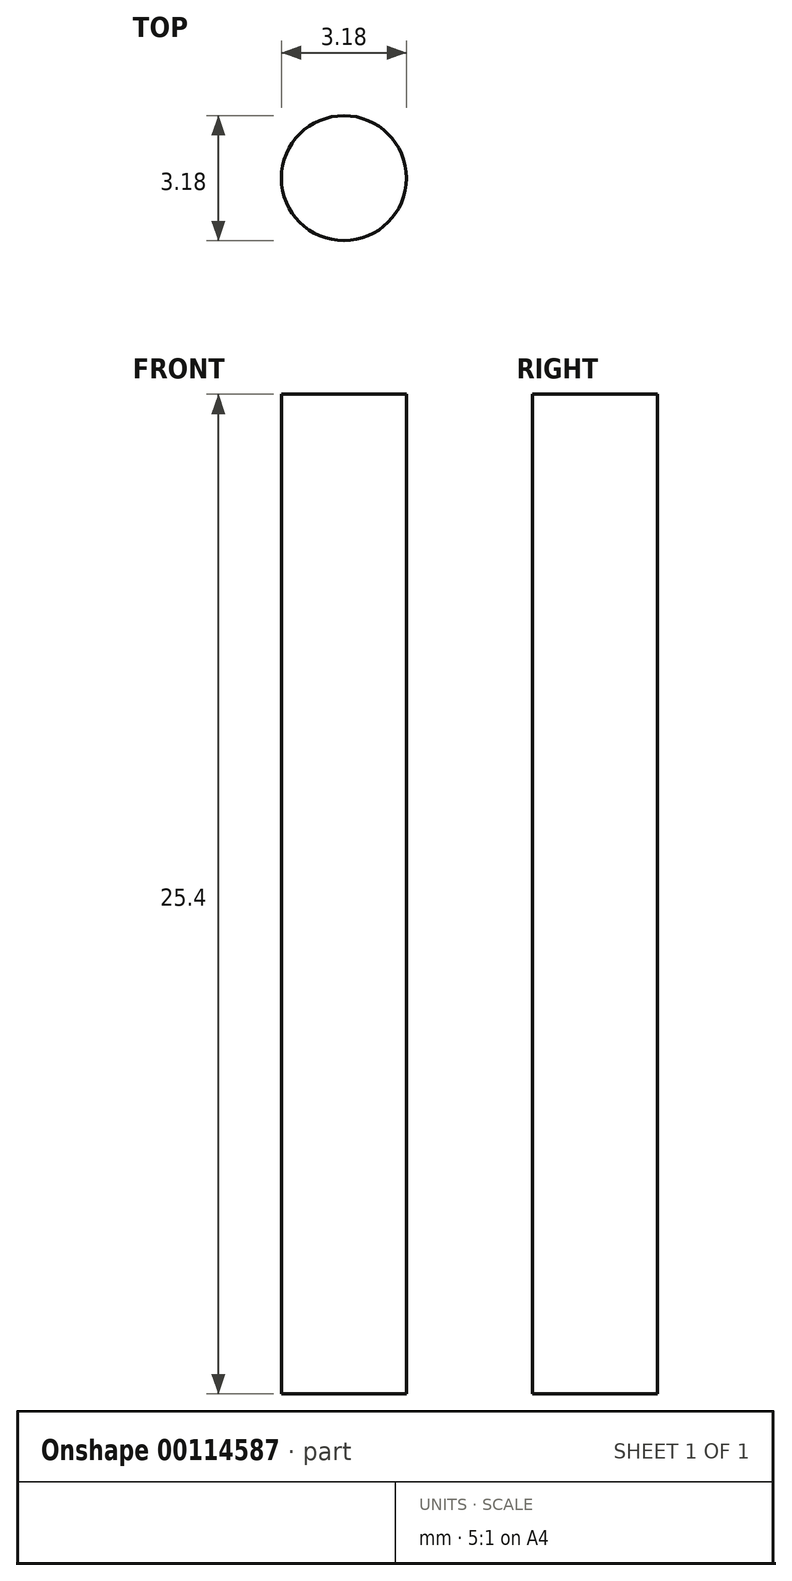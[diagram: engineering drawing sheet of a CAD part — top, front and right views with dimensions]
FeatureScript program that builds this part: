
annotation { "Feature Type Name" : "Feature", "Feature Type Description" : "" }
export const myFeature = defineFeature(function(context is Context, id is Id, definition is map)
    precondition{}
    {
        {
            var Q0;
            Q0=qCreatedBy(makeId("Top.planeOp"),FACE);
            var sketch = newSketch(context, id + "F0", { "sketchPlane" : qUnion([Q0])});
            skCircle(sketch, "E0", {"center": v(0, 0) * mm, "radius": 1.59 * mm});
            skSolve(sketch);
        }
        {
            var Q0;
            Q0=makeQuery(id+"F0.imprint","IMPRINT",FACE,{"disambiguationData":[TD([[makeQuery(id+"F0.imprint","IMPRINT",EDGE,{"derivedFrom":sQuery(id+"F0.wireOp",EDGE,"E0")}),1.0]])]});
            extrude(context, id + "F1", {"entities" : qUnion([Q0]), "depth" : 25.4 * mm});
        }
    });
